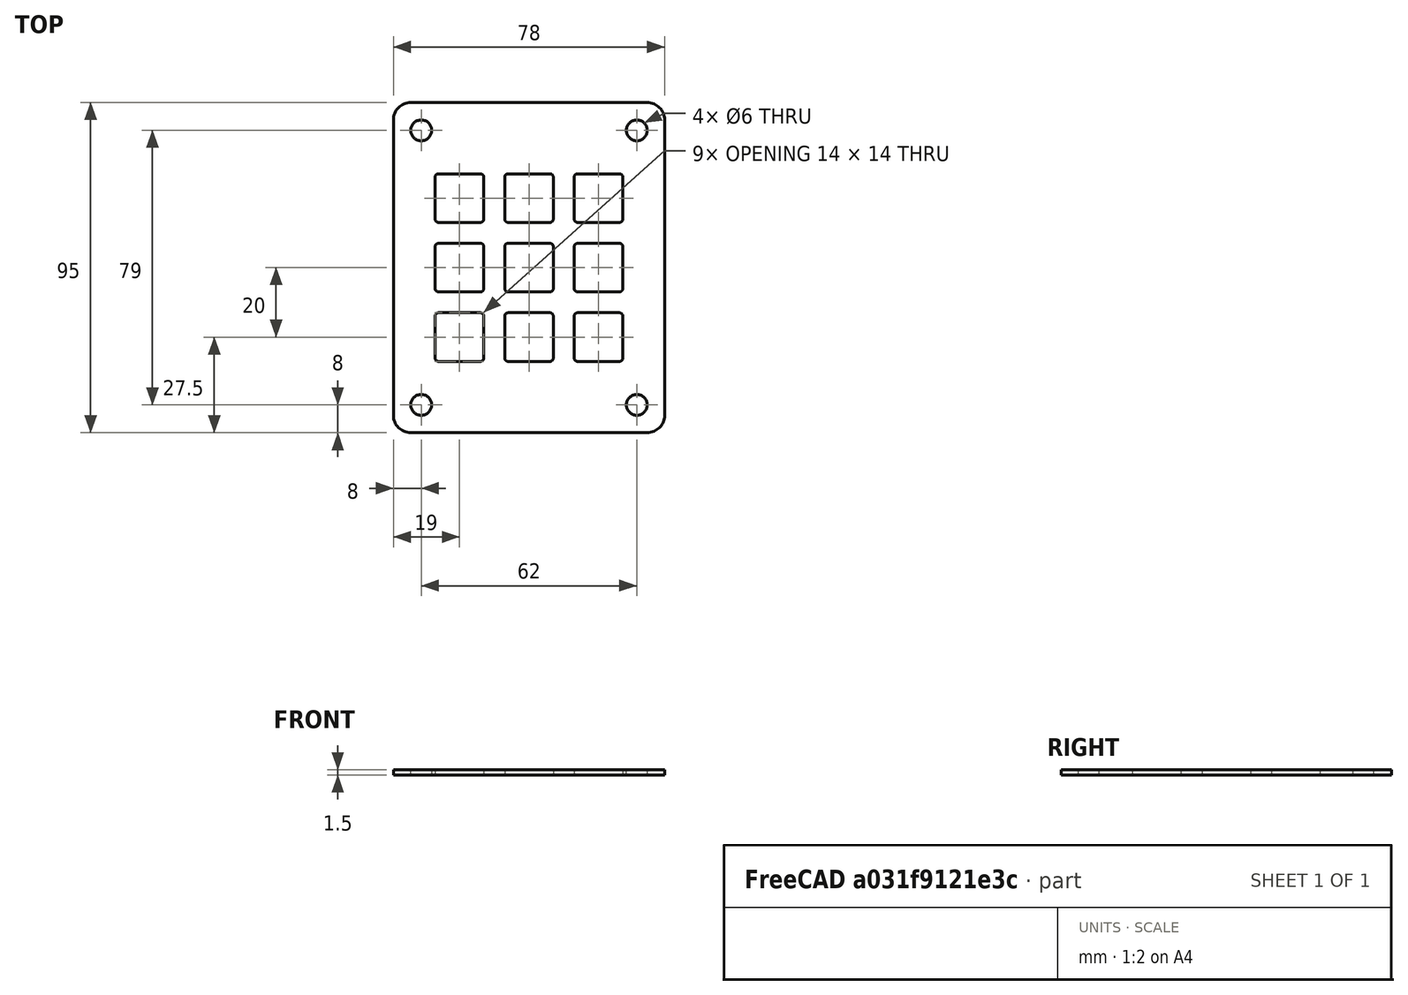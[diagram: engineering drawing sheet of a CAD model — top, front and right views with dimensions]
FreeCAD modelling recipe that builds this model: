
FCSTD DOCUMENT  (FreeCAD 1.0R39285 (Git))
Label: MetalFrame_proyect
License: All rights reserved
LicenseURL: https://en.wikipedia.org/wiki/All_rights_reserved
objects: TechDraw::DrawViewDimension×14, Sketcher::SketchObject×4, PartDesign::Pocket×2, PartDesign::Fillet×2, TechDraw::DrawProjGroupItem×2, TechDraw::DrawViewBalloon×2, PartDesign::Pad×1, PartDesign::Body×1, TechDraw::DrawSVGTemplate×1, TechDraw::DrawProjGroup×1, TechDraw::DrawViewAnnotation×1, TechDraw::DrawPage×1
note: 48 computed .brp shape members not serialized (recipe doc carries the construction recipe); baked Part::Feature solids carry a one-line shape summary decoded from their .brp

FEATURE [Sketcher::SketchObject] Sketch
  ArcFitTolerance = 1e-06
  AttachmentSupport = -> [XY_Plane]
  FullyConstrained = true
  MakeInternals = false
  MapMode = 5
  sketch-geometry (5):
    g0: LineSegment StartX=-39 StartY=-47.5 StartZ=0 EndX=39 EndY=-47.5 EndZ=0
    g1: LineSegment StartX=39 StartY=-47.5 StartZ=0 EndX=39 EndY=47.5 EndZ=0
    g2: LineSegment StartX=39 StartY=47.5 StartZ=0 EndX=-39 EndY=47.5 EndZ=0
    g3: LineSegment StartX=-39 StartY=47.5 StartZ=0 EndX=-39 EndY=-47.5 EndZ=0
    g4: GeomPoint [constr] X=0 Y=0 Z=0
  constraints (12):
    c: Coincident(g0,g1)
    c: Coincident(g1,g2)
    c: Coincident(g2,g3)
    c: Coincident(g3,g0)
    c: Horizontal(g0)
    c: Horizontal(g2)
    c: Vertical(g1)
    c: Vertical(g3)
    c: Symmetric(g2,g0,g4)
    c: Distance(g1,g3) = 78
    c: Distance(g0,g2) = 95
    c: Coincident(g4,g-1)
FEATURE [PartDesign::Pad] Pad
  Direction = (0,0,1)
  Length = 1.5
  Length2 = 10
  Profile = -> Sketch
  ReferenceAxis = -> Sketch [N_Axis]
  Refine = true
  Suppressed = false
  Type = 0
FEATURE [Sketcher::SketchObject] Sketch001
  ArcFitTolerance = 1e-06
  AttachmentSupport = -> [Pad]
  FullyConstrained = true
  MakeInternals = false
  MapMode = 5
  Placement = pos=(0,0,1.5) rot=(0,0,1;0rad)
FEATURE [Sketcher::SketchObject] Sketch002
  ArcFitTolerance = 1e-06
  AttachmentSupport = -> [Pad]
  ExternalGeometry = -> [Pad]
  FullyConstrained = true
  MakeInternals = false
  MapMode = 5
  Placement = pos=(0,0,1.5) rot=(0,0,1;0rad)
  sketch-geometry (47):
    g0: LineSegment StartX=-27 StartY=13 StartZ=0 EndX=-13 EndY=13 EndZ=0
    g1: LineSegment StartX=-13 StartY=13 StartZ=0 EndX=-13 EndY=27 EndZ=0
    g2: LineSegment StartX=-13 StartY=27 StartZ=0 EndX=-27 EndY=27 EndZ=0
    g3: LineSegment StartX=-27 StartY=27 StartZ=0 EndX=-27 EndY=13 EndZ=0
    g4: GeomPoint [constr] X=-20 Y=20 Z=0
    g5: LineSegment StartX=-7 StartY=27 StartZ=0 EndX=-7 EndY=13 EndZ=0
    g6: LineSegment StartX=-7 StartY=13 StartZ=0 EndX=7 EndY=13 EndZ=0
    g7: LineSegment StartX=7 StartY=13 StartZ=0 EndX=7 EndY=27 EndZ=0
    g8: LineSegment StartX=7 StartY=27 StartZ=0 EndX=-7 EndY=27 EndZ=0
    g9: GeomPoint [constr] X=7e-16 Y=20 Z=0
    g10: LineSegment StartX=13 StartY=27 StartZ=0 EndX=13 EndY=13 EndZ=0
    g11: LineSegment StartX=13 StartY=13 StartZ=0 EndX=27 EndY=13 EndZ=0
    g12: LineSegment StartX=27 StartY=13 StartZ=0 EndX=27 EndY=27 EndZ=0
    g13: LineSegment StartX=27 StartY=27 StartZ=0 EndX=13 EndY=27 EndZ=0
    g14: GeomPoint [constr] X=20 Y=20 Z=0
    g15: LineSegment StartX=-27 StartY=7 StartZ=0 EndX=-27 EndY=-7 EndZ=0
    g16: LineSegment StartX=-27 StartY=-7 StartZ=0 EndX=-13 EndY=-7 EndZ=0
    g17: LineSegment StartX=-13 StartY=-7 StartZ=0 EndX=-13 EndY=7 EndZ=0
    g18: LineSegment StartX=-13 StartY=7 StartZ=0 EndX=-27 EndY=7 EndZ=0
    g19: GeomPoint [constr] X=-20 Y=4.3e-15 Z=0
    g20: LineSegment StartX=-7 StartY=7 StartZ=0 EndX=-7 EndY=-7 EndZ=0
    g21: LineSegment StartX=-7 StartY=-7 StartZ=0 EndX=7 EndY=-7 EndZ=0
    g22: LineSegment StartX=7 StartY=-7 StartZ=0 EndX=7 EndY=7 EndZ=0
    g23: LineSegment StartX=7 StartY=7 StartZ=0 EndX=-7 EndY=7 EndZ=0
    g24: GeomPoint [constr] X=7e-16 Y=4.3e-15 Z=0
    g25: LineSegment StartX=13 StartY=7 StartZ=0 EndX=13 EndY=-7 EndZ=0
    g26: LineSegment StartX=13 StartY=-7 StartZ=0 EndX=27 EndY=-7 EndZ=0
    g27: LineSegment StartX=27 StartY=-7 StartZ=0 EndX=27 EndY=7 EndZ=0
    g28: LineSegment StartX=27 StartY=7 StartZ=0 EndX=13 EndY=7 EndZ=0
    g29: GeomPoint [constr] X=20 Y=4.3e-15 Z=0
    g30: LineSegment StartX=-27 StartY=-13 StartZ=0 EndX=-27 EndY=-27 EndZ=0
    g31: LineSegment StartX=-27 StartY=-27 StartZ=0 EndX=-13 EndY=-27 EndZ=0
    g32: LineSegment StartX=-13 StartY=-27 StartZ=0 EndX=-13 EndY=-13 EndZ=0
    g33: LineSegment StartX=-13 StartY=-13 StartZ=0 EndX=-27 EndY=-13 EndZ=0
    g34: GeomPoint [constr] X=-20 Y=-20 Z=0
    g35: LineSegment StartX=-7 StartY=-13 StartZ=0 EndX=-7 EndY=-27 EndZ=0
    g36: LineSegment StartX=-7 StartY=-27 StartZ=0 EndX=7 EndY=-27 EndZ=0
    g37: LineSegment StartX=7 StartY=-27 StartZ=0 EndX=7 EndY=-13 EndZ=0
    g38: LineSegment StartX=7 StartY=-13 StartZ=0 EndX=-7 EndY=-13 EndZ=0
    g39: GeomPoint [constr] X=7e-16 Y=-20 Z=0
    g40: LineSegment StartX=13 StartY=-13 StartZ=0 EndX=13 EndY=-27 EndZ=0
    g41: LineSegment StartX=13 StartY=-27 StartZ=0 EndX=27 EndY=-27 EndZ=0
    g42: LineSegment StartX=27 StartY=-27 StartZ=0 EndX=27 EndY=-13 EndZ=0
    g43: LineSegment StartX=27 StartY=-13 StartZ=0 EndX=13 EndY=-13 EndZ=0
    g44: GeomPoint [constr] X=20 Y=-20 Z=0
    g45: LineSegment [constr] StartX=-27 StartY=27 StartZ=0 EndX=-13 EndY=13 EndZ=0
    g46: LineSegment [constr] StartX=-13 StartY=27 StartZ=0 EndX=-27 EndY=13 EndZ=0
  constraints (121):
    c: Coincident(g0,g1)
    c: Coincident(g1,g2)
    c: Coincident(g2,g3)
    c: Coincident(g3,g0)
    c: Horizontal(g0)
    c: Horizontal(g2)
    c: Vertical(g1)
    c: Vertical(g3)
    c: Symmetric(g2,g0,g4)
    c: Distance(g1,g3) = 14
    c: Distance(g0,g2) = 14
    c: Coincident(g5,g6)
    c: Coincident(g6,g7)
    c: Coincident(g7,g8)
    c: Coincident(g8,g5)
    c: Vertical(g5)
    c: Vertical(g7)
    c: Horizontal(g6)
    c: Horizontal(g8)
    c: Symmetric(g7,g5,g9)
    c: Coincident(g10,g11)
    c: Coincident(g11,g12)
    c: Coincident(g12,g13)
    c: Coincident(g13,g10)
    c: Vertical(g10)
    c: Vertical(g12)
    c: Horizontal(g11)
    c: Horizontal(g13)
    c: Symmetric(g12,g10,g14)
    c: Coincident(g15,g16)
    c: Coincident(g16,g17)
    c: Coincident(g17,g18)
    c: Coincident(g18,g15)
    c: Vertical(g15)
    c: Vertical(g17)
    c: Horizontal(g16)
    c: Horizontal(g18)
    c: Symmetric(g17,g15,g19)
    c: Coincident(g20,g21)
    c: Coincident(g21,g22)
    c: Coincident(g22,g23)
    c: Coincident(g23,g20)
    c: Vertical(g20)
    c: Vertical(g22)
    c: Horizontal(g21)
    c: Horizontal(g23)
    c: Symmetric(g22,g20,g24)
    c: Coincident(g25,g26)
    c: Coincident(g26,g27)
    c: Coincident(g27,g28)
    c: Coincident(g28,g25)
    c: Vertical(g25)
    c: Vertical(g27)
    c: Horizontal(g26)
    c: Horizontal(g28)
    c: Symmetric(g27,g25,g29)
    c: Coincident(g30,g31)
    c: Coincident(g31,g32)
    c: Coincident(g32,g33)
    c: Coincident(g33,g30)
    c: Vertical(g30)
    c: Vertical(g32)
    c: Horizontal(g31)
    c: Horizontal(g33)
    c: Symmetric(g32,g30,g34)
    c: Coincident(g35,g36)
    c: Coincident(g36,g37)
    c: Coincident(g37,g38)
    c: Coincident(g38,g35)
    c: Vertical(g35)
    c: Vertical(g37)
    c: Horizontal(g36)
    c: Horizontal(g38)
    c: Symmetric(g37,g35,g39)
    c: Coincident(g40,g41)
    c: Coincident(g41,g42)
    c: Coincident(g42,g43)
    c: Coincident(g43,g40)
    c: Vertical(g40)
    c: Vertical(g42)
    c: Horizontal(g41)
    c: Horizontal(g43)
    c: Symmetric(g42,g40,g44)
    c: Horizontal(g4,g9)
    c: Horizontal(g9,g14)
    c: Horizontal(g19,g24)
    c: Horizontal(g24,g29)
    c: Horizontal(g34,g39)
    c: Horizontal(g39,g44)
    c: Vertical(g4,g19)
    c: Vertical(g19,g34)
    c: Vertical(g9,g24)
    c: Vertical(g24,g39)
    c: Vertical(g14,g29)
    c: Vertical(g29,g44)
    c: Equal(g2,g8)
    c: Equal(g5,g8)
    c: Equal(g8,g13)
    c: Equal(g13,g12)
    c: Equal(g0,g18)
    c: Equal(g18,g15)
    c: Equal(g17,g23)
    c: Equal(g23,g20)
    c: Equal(g22,g28)
    c: Equal(g28,g27)
    c: Equal(g33,g16)
    c: Equal(g30,g16)
    c: Equal(g21,g38)
    c: Equal(g35,g38)
    c: Equal(g26,g43)
    c: Equal(g41,g42)
    c: Distance(g4,g-3) = 19
    c: DistanceX(g4,g9) = 20
    c: Distance(g9,g14) = 20
    c: Distance(g4,g-4) = 27.5
    c: DistanceY(g19,g4) = 20
    c: DistanceY(g34,g19) = 20
    c: Coincident(g45,g2)
    c: Coincident(g45,g0)
    c: Coincident(g46,g1)
    c: Coincident(g46,g0)
FEATURE [PartDesign::Pocket] Pocket
  BaseFeature = -> Pad
  Direction = (0,0,-1)
  Length = 5
  Length2 = 5
  Profile = -> Sketch002
  ReferenceAxis = -> Sketch002 [N_Axis]
  Refine = true
  Suppressed = false
  Type = 1
FEATURE [PartDesign::Fillet] Fillet
  Base = -> Pocket [Edge104,Edge98,Edge86,Edge114,Edge106,Edge90,Edge94,Edge110,Edge118,Edge103,Edge116,Edge120,Edge100,Edge108,Edge112,Edge88,Edge92,Edge96,Edge119,Edge115,Edge101,Edge111,Edge107,Edge99,Edge95,Edge91,Edge87,Edge93,Edge89,Edge85,Edge109,Edge105,Edge97,Edge117,Edge113,Edge102]
  BaseFeature = -> Pocket
  Radius = 1
  Refine = true
  SupportTransform = false
  Suppressed = false
  UseAllEdges = false
FEATURE [Sketcher::SketchObject] Sketch003
  ArcFitTolerance = 1e-06
  AttachmentSupport = -> [Fillet]
  ExternalGeometry = -> [Fillet]
  FullyConstrained = true
  MakeInternals = false
  MapMode = 5
  Placement = pos=(0,0,1.5) rot=(0,0,1;0rad)
  sketch-geometry (4):
    g0: Circle CenterX=-31 CenterY=39.5 CenterZ=0 NormalX=0 NormalY=0 NormalZ=1 AngleXU=0 Radius=3
    g1: Circle CenterX=31 CenterY=39.5 CenterZ=0 NormalX=0 NormalY=0 NormalZ=1 AngleXU=0 Radius=3
    g2: Circle CenterX=31 CenterY=-39.5 CenterZ=0 NormalX=0 NormalY=0 NormalZ=1 AngleXU=0 Radius=3
    g3: Circle CenterX=-31 CenterY=-39.5 CenterZ=0 NormalX=0 NormalY=0 NormalZ=1 AngleXU=0 Radius=3
  constraints (12):
    c: Diameter(g0) = 6
    c: Equal(g0,g1)
    c: Equal(g1,g2)
    c: Equal(g2,g3)
    c: Horizontal(g0,g1)
    c: Horizontal(g3,g2)
    c: Vertical(g0,g3)
    c: Vertical(g2,g1)
    c: Distance(g0,g-3) = 8
    c: Distance(g0,g-4) = 8
    c: Distance(g3,g-5) = 8
    c: Distance(g1,g-6) = 8
FEATURE [PartDesign::Pocket] Pocket001
  BaseFeature = -> Fillet
  Direction = (0,0,-1)
  Length = 5
  Length2 = 5
  Profile = -> Sketch003
  ReferenceAxis = -> Sketch003 [N_Axis]
  Refine = true
  Suppressed = false
  Type = 1
FEATURE [PartDesign::Fillet] Fillet001
  Base = -> Pocket001 [Edge82,Edge81,Edge84,Edge86]
  BaseFeature = -> Pocket001
  Radius = 5
  Refine = true
  SupportTransform = false
  Suppressed = false
  UseAllEdges = false
FEATURE [PartDesign::Body] Body
  AllowCompound = false
  Group = -> [Sketch,Pad,Sketch001,Sketch002,Pocket,Fillet,Sketch003,Pocket001,Fillet001]
  Origin = -> Origin
  Tip = -> Fillet001
FEATURE [TechDraw::DrawSVGTemplate] Template
  Height = 210
  Orientation = 1
  Template = <path>
  Width = 297
FEATURE [TechDraw::DrawProjGroupItem] View  label="Front"
  CoarseView = false
  Direction = (0,0,-1)
  Focus = 100
  HardHidden = false
  IsoCount = 0
  IsoHidden = false
  IsoVisible = false
  LockPosition = true
  Perspective = false
  Rotation = 0
  RotationVector = (1,0,0)
  ScaleType = 2
  ScrubCount = 1
  SeamHidden = false
  SeamVisible = false
  SmoothHidden = false
  SmoothVisible = true
  Source = -> [Body]
  Type = 0
  X = 0
  XDirection = (1,0,0)
  Y = 0
FEATURE [TechDraw::DrawProjGroupItem] ProjItem  label="Left"
  CoarseView = false
  Direction = (-1,0,-1e-16)
  Focus = 100
  HardHidden = false
  IsoCount = 0
  IsoHidden = false
  IsoVisible = false
  LockPosition = false
  Perspective = false
  Rotation = 0
  RotationVector = (1,0,0)
  ScaleType = 0
  ScrubCount = 1
  SeamHidden = false
  SeamVisible = false
  SmoothHidden = false
  SmoothVisible = true
  Source = -> [Body]
  Type = 1
  X = 54.75
  XDirection = (1e-16,0,-1)
  Y = 0
FEATURE [TechDraw::DrawProjGroup] ProjGroup
  Anchor = -> View
  AutoDistribute = true
  LockPosition = false
  ProjectionType = 0
  Rotation = 0
  ScaleType = 0
  Source = -> [Body]
  Views = -> [View,ProjItem]
  X = 152.467
  Y = 105.7
  spacingX = 15
  spacingY = 15
FEATURE [TechDraw::DrawViewDimension] Dimension
  AngleOverride = false
  Arbitrary = false
  ArbitraryTolerances = false
  BoxCorners = (2) [(-39,-47.5,0),(39,47.5,0)]
  EqualTolerance = true
  ExtensionAngle = 0
  FormatSpec = %.2w
  FormatSpecOverTolerance = %+.2w
  FormatSpecUnderTolerance = %+.2w
  Inverted = false
  LineAngle = 0
  LockPosition = false
  MeasureType = 1
  OverTolerance = 0
  References2D = -> [View]
  Rotation = 0
  ScaleType = 0
  TheoreticalExact = false
  Type = 1
  UnderTolerance = 0
  X = 0
  Y = 73.2964
FEATURE [TechDraw::DrawViewDimension] Dimension001
  AngleOverride = false
  Arbitrary = false
  ArbitraryTolerances = false
  BoxCorners = (2) [(-39,-47.5,0),(39,47.5,0)]
  EqualTolerance = true
  ExtensionAngle = 0
  FormatSpec = %.2w
  FormatSpecOverTolerance = %+.2w
  FormatSpecUnderTolerance = %+.2w
  Inverted = false
  LineAngle = 0
  LockPosition = false
  MeasureType = 1
  OverTolerance = 0
  References2D = -> [View]
  Rotation = 0
  ScaleType = 0
  TheoreticalExact = false
  Type = 2
  UnderTolerance = 0
  X = -68.9236
  Y = 0
FEATURE [TechDraw::DrawViewDimension] Dimension004
  AngleOverride = false
  Arbitrary = false
  ArbitraryTolerances = false
  BoxCorners = (2) [(-39,-47.5,0),(39,47.5,0)]
  EqualTolerance = true
  ExtensionAngle = 0
  FormatSpec = %.2w
  FormatSpecOverTolerance = %+.2w
  FormatSpecUnderTolerance = %+.2w
  Inverted = false
  LineAngle = 0
  LockPosition = false
  MeasureType = 1
  OverTolerance = 0.05
  References2D = -> [View]
  Rotation = 0
  ScaleType = 0
  TheoreticalExact = false
  Type = 1
  UnderTolerance = -0.05
  X = -19.25
  Y = 59.0268
FEATURE [TechDraw::DrawViewDimension] Dimension005
  AngleOverride = false
  Arbitrary = false
  ArbitraryTolerances = false
  BoxCorners = (2) [(-39,-47.5,0),(39,47.5,0)]
  EqualTolerance = true
  ExtensionAngle = 0
  FormatSpec = %.2w
  FormatSpecOverTolerance = %+.2w
  FormatSpecUnderTolerance = %+.2w
  Inverted = false
  LineAngle = 0
  LockPosition = false
  MeasureType = 1
  OverTolerance = 0.05
  References2D = -> [View]
  Rotation = 0
  ScaleType = 0
  TheoreticalExact = false
  Type = 2
  UnderTolerance = -0.05
  X = -50.7043
  Y = 20
FEATURE [TechDraw::DrawViewDimension] Dimension007
  AngleOverride = false
  Arbitrary = false
  ArbitraryTolerances = false
  BoxCorners = (2) [(-39,-47.5,0),(39,47.5,0)]
  EqualTolerance = true
  ExtensionAngle = 0
  FormatSpec = ⌀%.2w
  FormatSpecOverTolerance = %+.2w
  FormatSpecUnderTolerance = %+.2w
  Inverted = false
  LineAngle = 0
  LockPosition = false
  MeasureType = 1
  OverTolerance = 0
  References2D = -> [View]
  Rotation = 0
  ScaleType = 0
  TheoreticalExact = false
  Type = 5
  UnderTolerance = 0
  X = 21.4146
  Y = 41.1211
FEATURE [TechDraw::DrawViewDimension] Dimension008
  AngleOverride = false
  Arbitrary = false
  ArbitraryTolerances = false
  BoxCorners = (2) [(-39,-47.5,0),(39,47.5,0)]
  EqualTolerance = true
  ExtensionAngle = 0
  FormatSpec = R%.2w
  FormatSpecOverTolerance = %+.2w
  FormatSpecUnderTolerance = %+.2w
  Inverted = false
  LineAngle = 0
  LockPosition = false
  MeasureType = 1
  OverTolerance = 0
  References2D = -> [View]
  Rotation = 0
  ScaleType = 0
  TheoreticalExact = false
  Type = 4
  UnderTolerance = 0
  X = 47.2836
  Y = 58.0511
FEATURE [TechDraw::DrawViewDimension] Dimension009
  AngleOverride = false
  Arbitrary = false
  ArbitraryTolerances = false
  BoxCorners = (2) [(-39,-47.5,0),(39,47.5,0)]
  EqualTolerance = true
  ExtensionAngle = 0
  FormatSpec = %.2w
  FormatSpecOverTolerance = %+.2w
  FormatSpecUnderTolerance = %+.2w
  Inverted = false
  LineAngle = 0
  LockPosition = false
  MeasureType = 1
  OverTolerance = 0
  References2D = -> [View]
  Rotation = 0
  ScaleType = 0
  TheoreticalExact = false
  Type = 0
  UnderTolerance = 0
  X = -35
  Y = -51.0772
FEATURE [TechDraw::DrawViewDimension] Dimension010
  AngleOverride = false
  Arbitrary = false
  ArbitraryTolerances = false
  BoxCorners = (2) [(-39,-47.5,0),(39,47.5,0)]
  EqualTolerance = true
  ExtensionAngle = 0
  FormatSpec = %.2w
  FormatSpecOverTolerance = %+.2w
  FormatSpecUnderTolerance = %+.2w
  Inverted = false
  LineAngle = 0
  LockPosition = false
  MeasureType = 1
  OverTolerance = 0
  References2D = -> [View]
  Rotation = 0
  ScaleType = 0
  TheoreticalExact = false
  Type = 0
  UnderTolerance = 0
  X = -55.553
  Y = -43.5
FEATURE [TechDraw::DrawViewDimension] Dimension011
  AngleOverride = false
  Arbitrary = false
  ArbitraryTolerances = false
  BoxCorners = (2) [(-0.75,-47.5,-1e-07),(0.75,47.5,1e-07)]
  EqualTolerance = true
  ExtensionAngle = 0
  FormatSpec = %.2w
  FormatSpecOverTolerance = %+.2w
  FormatSpecUnderTolerance = %+.2w
  Inverted = false
  LineAngle = 0
  LockPosition = false
  MeasureType = 1
  OverTolerance = 0.1
  References2D = -> [ProjItem]
  Rotation = 0
  ScaleType = 0
  TheoreticalExact = false
  Type = 0
  UnderTolerance = -0.1
  X = 10.4686
  Y = 73.2438
FEATURE [TechDraw::DrawViewBalloon] Balloon001
  BubbleShape = 1
  EndType = 0
  EndTypeScale = 1
  KinkLength = 5
  LockPosition = false
  OriginX = -19.2833
  OriginY = 19.6728
  Rotation = 0
  ScaleType = 0
  ShapeScale = 1
  SourceView = -> View
  Text = All square holes are the same
  TextWrapLen = -1
  X = -103.293
  Y = 63.4986
FEATURE [TechDraw::DrawViewBalloon] Balloon
  BubbleShape = 1
  EndType = 0
  EndTypeScale = 1
  KinkLength = 5
  LockPosition = false
  OriginX = 31.0959
  OriginY = 39.4811
  Rotation = 0
  ScaleType = 0
  ShapeScale = 1
  SourceView = -> View
  Text = All circle holes are the same
  TextWrapLen = -1
  X = 46.8048
  Y = 81.6517
FEATURE [TechDraw::DrawViewDimension] Dimension012
  AngleOverride = false
  Arbitrary = false
  ArbitraryTolerances = false
  BoxCorners = (2) [(-39,-47.5,0),(39,47.5,0)]
  EqualTolerance = true
  ExtensionAngle = 0
  FormatSpec = %.2w
  FormatSpecOverTolerance = %+.2w
  FormatSpecUnderTolerance = %+.2w
  Inverted = false
  LineAngle = 0
  LockPosition = false
  MeasureType = 1
  OverTolerance = 0
  References2D = -> [View]
  Rotation = 0
  ScaleType = 0
  TheoreticalExact = false
  Type = 0
  UnderTolerance = 0
  X = -33
  Y = -63.5999
FEATURE [TechDraw::DrawViewDimension] Dimension013
  AngleOverride = false
  Arbitrary = false
  ArbitraryTolerances = false
  BoxCorners = (2) [(-39,-47.5,0),(39,47.5,0)]
  EqualTolerance = true
  ExtensionAngle = 0
  FormatSpec = %.2w
  FormatSpecOverTolerance = %+.2w
  FormatSpecUnderTolerance = %+.2w
  Inverted = false
  LineAngle = 0
  LockPosition = false
  MeasureType = 1
  OverTolerance = 0
  References2D = -> [View]
  Rotation = 0
  ScaleType = 0
  TheoreticalExact = false
  Type = 0
  UnderTolerance = 0
  X = -10
  Y = -63.5999
FEATURE [TechDraw::DrawViewDimension] Dimension014
  AngleOverride = false
  Arbitrary = false
  ArbitraryTolerances = false
  BoxCorners = (2) [(-39,-47.5,0),(39,47.5,0)]
  EqualTolerance = true
  ExtensionAngle = 0
  FormatSpec = %.2w
  FormatSpecOverTolerance = %+.2w
  FormatSpecUnderTolerance = %+.2w
  Inverted = false
  LineAngle = 0
  LockPosition = false
  MeasureType = 1
  OverTolerance = 0
  References2D = -> [View]
  Rotation = 0
  ScaleType = 0
  TheoreticalExact = false
  Type = 0
  UnderTolerance = 0
  X = 10
  Y = -63.5999
FEATURE [TechDraw::DrawViewDimension] Dimension015
  AngleOverride = false
  Arbitrary = false
  ArbitraryTolerances = false
  BoxCorners = (2) [(-39,-47.5,0),(39,47.5,0)]
  EqualTolerance = true
  ExtensionAngle = 0
  FormatSpec = %.2w
  FormatSpecOverTolerance = %+.2w
  FormatSpecUnderTolerance = %+.2w
  Inverted = false
  LineAngle = 0
  LockPosition = false
  MeasureType = 1
  OverTolerance = 0
  References2D = -> [View]
  Rotation = 0
  ScaleType = 0
  TheoreticalExact = false
  Type = 0
  UnderTolerance = 0
  X = 33
  Y = -63.5999
FEATURE [TechDraw::DrawViewDimension] Dimension006
  AngleOverride = false
  Arbitrary = false
  ArbitraryTolerances = false
  BoxCorners = (2) [(-39,-47.5,0),(39,47.5,0)]
  EqualTolerance = true
  ExtensionAngle = 0
  FormatSpec = R%.2w
  FormatSpecOverTolerance = %+.2w
  FormatSpecUnderTolerance = %+.2w
  Inverted = false
  LineAngle = 0
  LockPosition = false
  MeasureType = 1
  OverTolerance = 0.05
  References2D = -> [View]
  Rotation = 0
  ScaleType = 0
  TheoreticalExact = false
  Type = 4
  UnderTolerance = -0.05
  X = 1.69969
  Y = 40.531
FEATURE [TechDraw::DrawViewAnnotation] Annotation
  Font = osifont
  LineSpace = 100
  LockPosition = false
  MaxWidth = -1
  Rotation = 0
  ScaleType = 0
  Text = *All units are in mm
  TextSize = 5
  TextStyle = 0
  X = 249.566
  Y = 15.1621
FEATURE [TechDraw::DrawPage] Page
  KeepUpdated = true
  NextBalloonIndex = 4
  ProjectionType = 0
  Template = -> Template
  Views = -> [ProjGroup,Dimension,Dimension001,Dimension004,Dimension005,Dimension006,Dimension007,Dimension008,Dimension009,Dimension010,Dimension011,Balloon001,Balloon,Dimension012,Dimension013,Dimension014,Dimension015,Annotation]
note: 1 file-system path scrubbed to <path> (originals preserved in the JSON sidecar)
